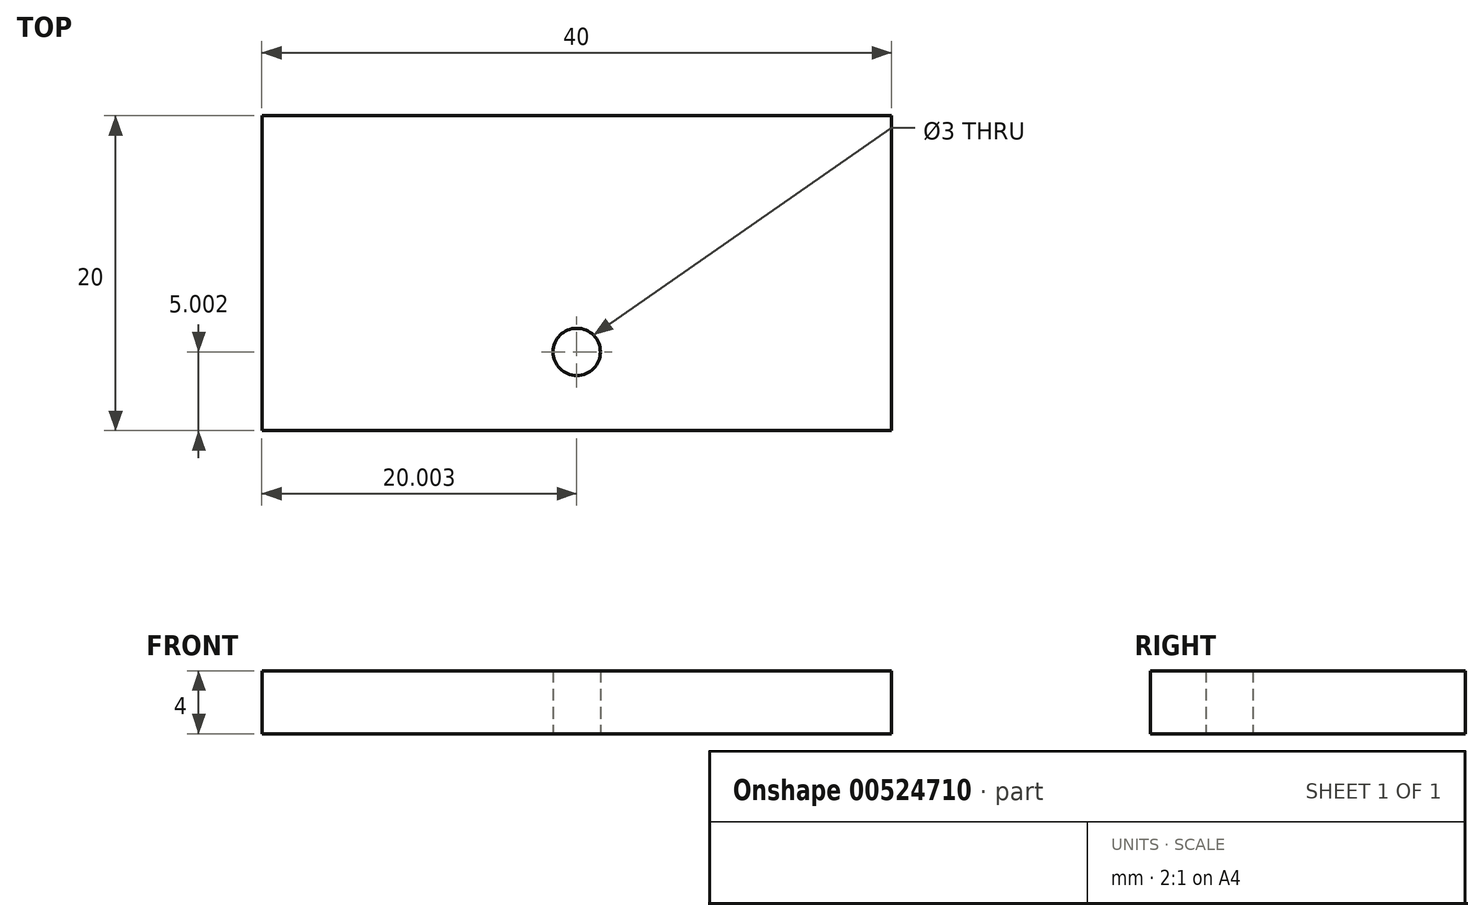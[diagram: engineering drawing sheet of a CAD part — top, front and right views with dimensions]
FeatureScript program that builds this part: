
annotation { "Feature Type Name" : "Feature", "Feature Type Description" : "" }
export const myFeature = defineFeature(function(context is Context, id is Id, definition is map)
    precondition{}
    {
        {
            var Q0;
            Q0=qCreatedBy(makeId("Top.planeOp"),FACE);
            var sketch = newSketch(context, id + "F0", { "sketchPlane" : qUnion([Q0])});
            skLineSegment(sketch, "E0.bottom", {"start": v(-28.82, 2.12) * mm, "end": v(11.18, 2.12) * mm});
            skLineSegment(sketch, "E0.top", {"start": v(-28.82, -17.88) * mm, "end": v(11.18, -17.88) * mm});
            skLineSegment(sketch, "E0.left", {"start": v(-28.82, 2.12) * mm, "end": v(-28.82, -17.88) * mm});
            skLineSegment(sketch, "E0.right", {"start": v(11.18, 2.12) * mm, "end": v(11.18, -17.88) * mm});
            skCircle(sketch, "E1", {"center": v(-8.82, -12.88) * mm, "radius": 1.5 * mm});
            skPoint(sketch, "E1.centerSnap0", {"position": v(-8.82, -17.88) * mm});
            skSolve(sketch);
        }
        {
            var Q0;
            Q0=makeQuery(id+"F0.imprint","IMPRINT",FACE,{"disambiguationData":[TD([[makeQuery(id+"F0.imprint","IMPRINT",EDGE,{"derivedFrom":sQuery(id+"F0.wireOp",EDGE,"E0.bottom")}),-1.0]])]});
            extrude(context, id + "F1", {"entities" : qUnion([Q0]), "depth" : 4 * mm, "offsetDistance" : 25 * mm});
        }
    });
